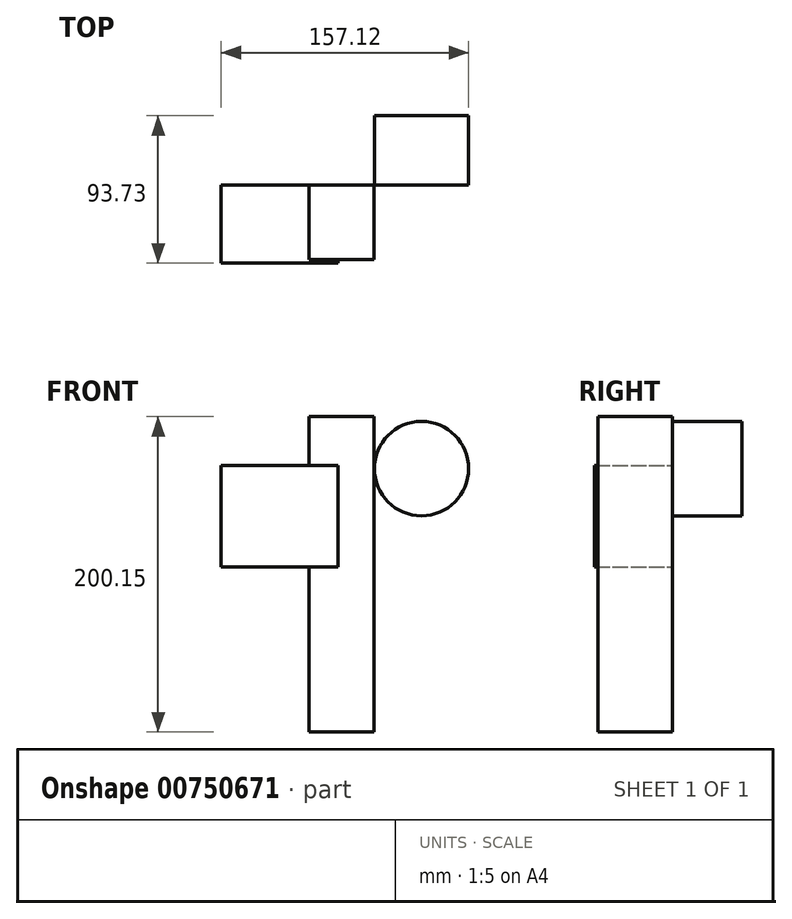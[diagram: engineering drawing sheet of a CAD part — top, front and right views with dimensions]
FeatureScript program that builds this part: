
annotation { "Feature Type Name" : "Feature", "Feature Type Description" : "" }
export const myFeature = defineFeature(function(context is Context, id is Id, definition is map)
    precondition{}
    {
        {
            var Q0;
            Q0=qCreatedBy(makeId("Front.planeOp"),FACE);
            var sketch = newSketch(context, id + "F0", { "sketchPlane" : qUnion([Q0])});
            skLineSegment(sketch, "E0.bottom", {"start": v(-55.7, 45.23) * mm, "end": v(18.57, 45.23) * mm});
            skLineSegment(sketch, "E0.top", {"start": v(-55.7, -19.16) * mm, "end": v(18.57, -19.16) * mm});
            skLineSegment(sketch, "E0.left", {"start": v(-55.7, 45.23) * mm, "end": v(-55.7, -19.16) * mm});
            skLineSegment(sketch, "E0.right", {"start": v(18.57, 45.23) * mm, "end": v(18.57, -19.16) * mm});
            skSolve(sketch);
        }
        {
            var Q0;
            Q0=makeQuery(id+"F0.imprint","IMPRINT",FACE,{"disambiguationData":[TD([[makeQuery(id+"F0.imprint","IMPRINT",EDGE,{"derivedFrom":sQuery(id+"F0.wireOp",EDGE,"E0.bottom")}),-1.0]])]});
            extrude(context, id + "F1", {"entities" : qUnion([Q0]), "depth" : 49.53 * mm, "offsetDistance" : 25.4 * mm});
        }
        {
            var Q0;
            Q0=qCreatedBy(makeId("Front.planeOp"),FACE);
            var sketch = newSketch(context, id + "F2", { "sketchPlane" : qUnion([Q0])});
            skLineSegment(sketch, "E1.bottom", {"start": v(41.16, 76.15) * mm, "end": v(0, 76.15) * mm});
            skLineSegment(sketch, "E1.top", {"start": v(41.16, -124) * mm, "end": v(0, -124) * mm});
            skLineSegment(sketch, "E1.left", {"start": v(41.16, 76.15) * mm, "end": v(41.16, -124) * mm});
            skLineSegment(sketch, "E1.right", {"start": v(0, 76.15) * mm, "end": v(0, -124) * mm});
            skSolve(sketch);
        }
        {
            var Q0;
            Q0=makeQuery(id+"F2.imprint","IMPRINT",FACE,{"disambiguationData":[TD([[makeQuery(id+"F2.imprint","IMPRINT",EDGE,{"derivedFrom":sQuery(id+"F2.wireOp",EDGE,"E1.bottom")}),1.0]])]});
            extrude(context, id + "F3", {"entities" : qUnion([Q0]), "operationType" : NewBodyOperationType.ADD, "depth" : 47.24 * mm, "offsetDistance" : 25.4 * mm});
        }
        {
            var Q0;
            Q0=qCreatedBy(makeId("Front.planeOp"),FACE);
            var sketch = newSketch(context, id + "F4", { "sketchPlane" : qUnion([Q0])});
            skCircle(sketch, "E2", {"center": v(71.47, 43.18) * mm, "radius": 29.95 * mm});
            skSolve(sketch);
        }
        {
            var Q0;
            Q0 = qSketchRegion(id + "F4", true);
            extrude(context, id + "F5", {"entities" : qUnion([Q0]), "oppositeDirection" : true, "depth" : 44.2 * mm, "offsetDistance" : 25.4 * mm});
        }
    });
